# Revit family: Parking_Optio-PGM-Parking-Garage-Monitor_Conspec
name_source: partatom
category: Generic Models
units: mm (PartAtom-declared; Revit-internal decimal feet)

## family parameters
Always vertical = Yes
Can host rebar = No
Cut with Voids When Loaded = No
Maintain Annotation Orientation = No
Part Type = Normal
Room Calculation Point = No
Round Connector Dimension = Use Diameter
Shared = No
Work Plane-Based = No

## types (1)
- Parking_Optio-PGM-Parking-Garage-Monitor_Conspec
    Default Elevation = 0 mm  [stored 0 ft]
    Depth = 130 mm  [stored 0.426509 ft]
    Description = Parking Garage Monitor
    Height = 71.24 mm
    Keynote = 26 09 00
    Manufacturer = Conspec
    Model = Optio PGM
    URL = https://www.arcat.com
    Width = 84 mm  [stored 0.275591 ft]

note: [stored X ft] marks values corroborated as IEEE doubles in the binary element streams (Revit-internal decimal feet)

## geometry (parser evidence)
native form markers: Sweep x2
no freeform markers — native parametric forms only
